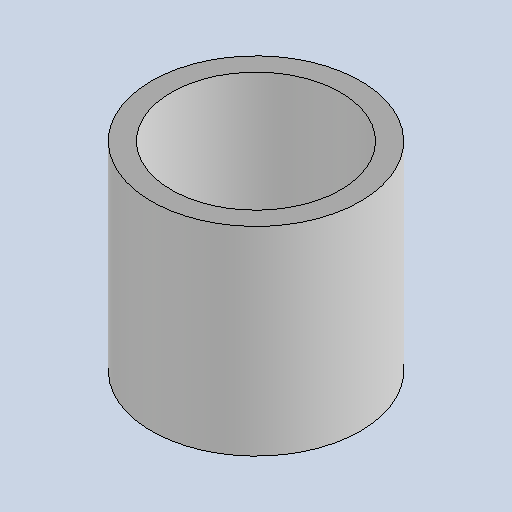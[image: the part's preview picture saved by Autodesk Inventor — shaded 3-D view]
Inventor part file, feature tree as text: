
AUTODESK INVENTOR PART (.ipt)
format: ipt  version: 2025.1 (Build 291241020, 241B)  size: 125,952 bytes
history: native  units: mm
features: extrude x1, sketch x1
ambient origin geometry x8: Origin, YZ Plane, XZ Plane, XY Plane, X Axis, Y Axis, Z Axis, Center Point
bodies: Body1 (feature_tree)
feature tree (2):
  extrude  "Extrusion5"  Depth=20.0mm
  sketch  "Sketch11"  dims[d187=21.0mm d188=2.0mm d189=20.0mm d190=0.0mm]
